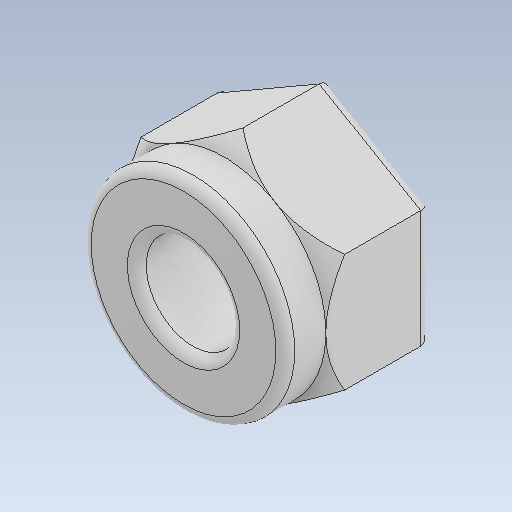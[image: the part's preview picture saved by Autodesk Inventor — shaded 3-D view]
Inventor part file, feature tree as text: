
AUTODESK INVENTOR PART (.ipt)
format: ipt  version: 2020 (Build 240168000, 168)  size: 158,720 bytes
history: native  units: in
note: dims shown in document units (in); Inventor stores cm internally (conversion verified against a paired STEP export)
features: fillet x1
ambient origin geometry x8: Origin, YZ Plane, XZ Plane, XY Plane, X Axis, Y Axis, Z Axis, Center Point
bodies: Solid1 (feature_tree)
feature tree (1):
  fillet  "Fillet4"  [1 undecoded]
note: 1 required parameter value undecoded (feature->parameter linkage not recoverable at this tier; creation-order binding heuristic only, values carry confidence <= 0.55)
